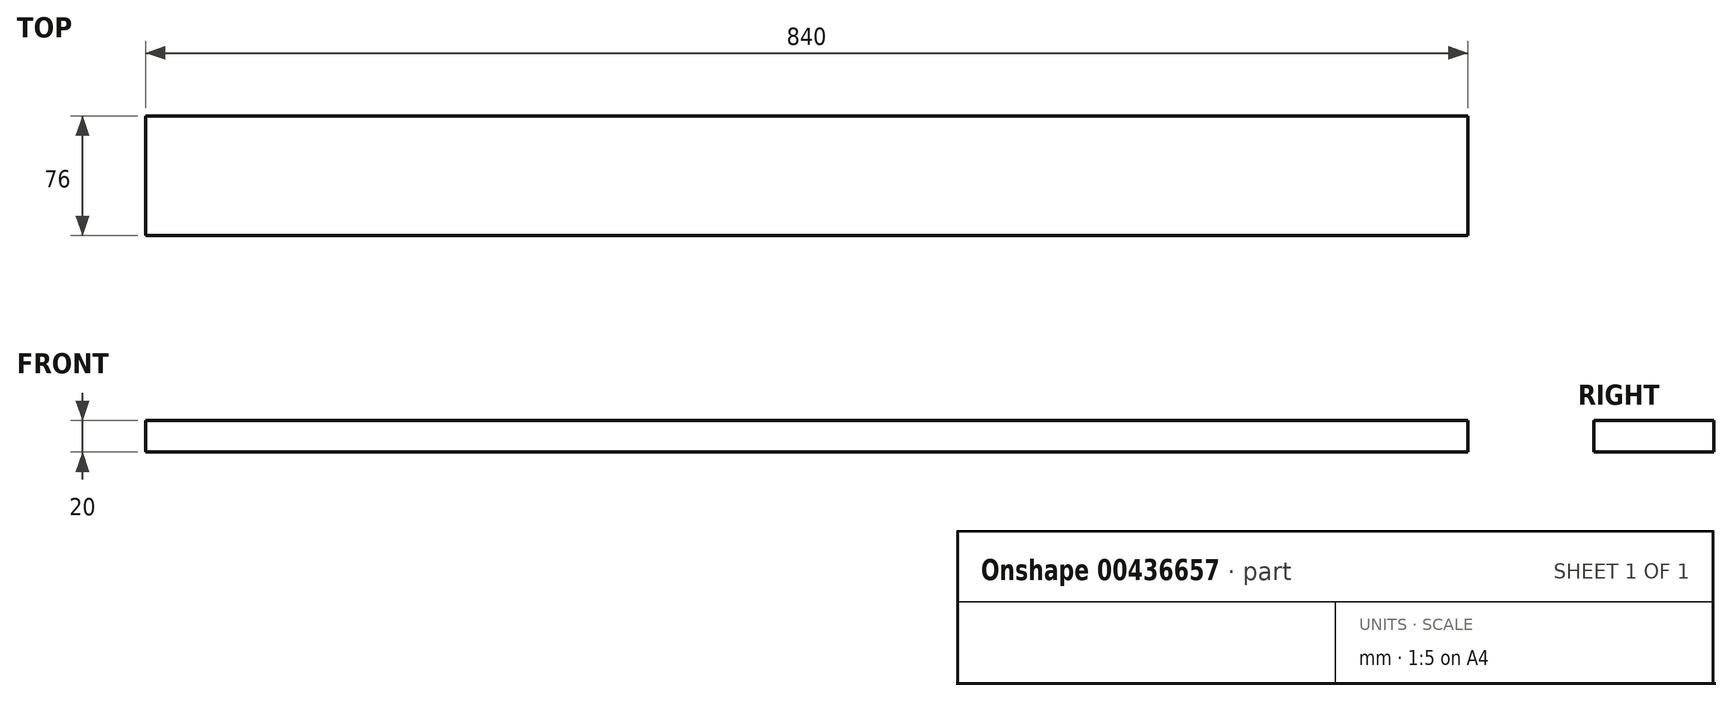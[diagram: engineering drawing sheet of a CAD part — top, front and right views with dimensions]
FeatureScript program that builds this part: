
annotation { "Feature Type Name" : "Feature", "Feature Type Description" : "" }
export const myFeature = defineFeature(function(context is Context, id is Id, definition is map)
    precondition{}
    {
        {
            var Q0;
            Q0=qCreatedBy(makeId("Right.planeOp"),FACE);
            var sketch = newSketch(context, id + "F0", { "sketchPlane" : qUnion([Q0])});
            skLineSegment(sketch, "E0.bottom", {"start": v(38, 10) * mm, "end": v(-38, 10) * mm});
            skLineSegment(sketch, "E0.top", {"start": v(38, -10) * mm, "end": v(-38, -10) * mm});
            skLineSegment(sketch, "E0.left", {"start": v(38, 10) * mm, "end": v(38, -10) * mm});
            skLineSegment(sketch, "E0.right", {"start": v(-38, 10) * mm, "end": v(-38, -10) * mm});
            skPoint(sketch, "E0.middle", {"position": v(0, 0) * mm});
            skSolve(sketch);
        }
        {
            var Q0;
            Q0=qSketchRegion(id+"F0",true);
            extrude(context, id + "F1", {"entities" : qUnion([Q0]), "depth" : 840 * mm});
        }
    });
